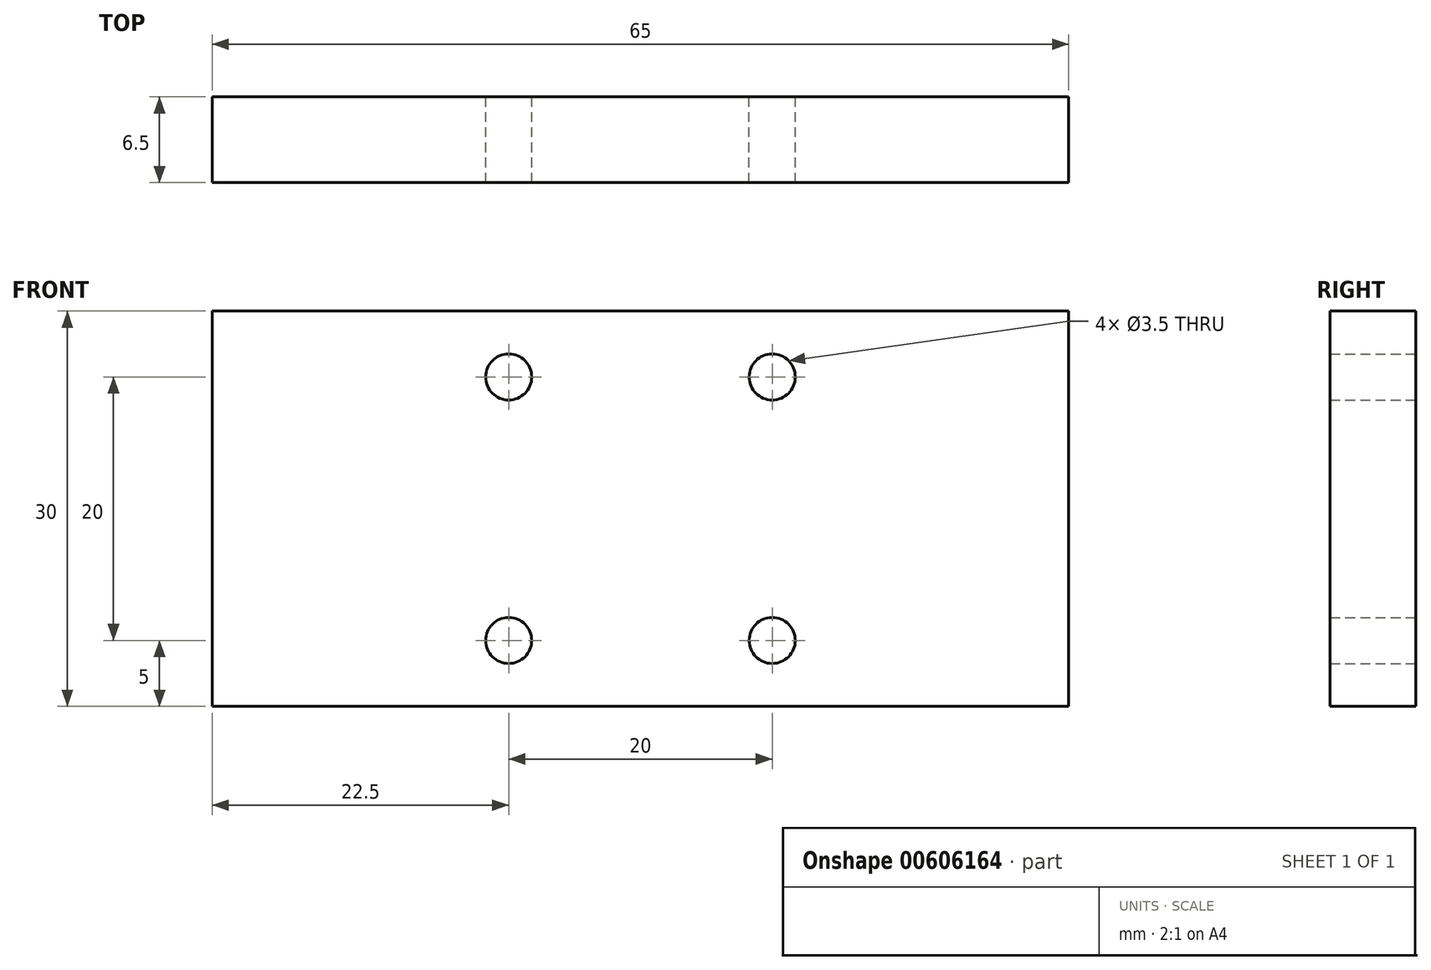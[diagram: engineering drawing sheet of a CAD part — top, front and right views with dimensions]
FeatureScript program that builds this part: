
annotation { "Feature Type Name" : "Feature", "Feature Type Description" : "" }
export const myFeature = defineFeature(function(context is Context, id is Id, definition is map)
    precondition{}
    {
        {
            var Q0;
            Q0=qCreatedBy(makeId("Front.planeOp"),FACE);
            var sketch = newSketch(context, id + "F0", { "sketchPlane" : qUnion([Q0])});
            skLineSegment(sketch, "E0.bottom", {"start": v(32.5, -15) * mm, "end": v(-32.5, -15) * mm});
            skLineSegment(sketch, "E0.top", {"start": v(32.5, 15) * mm, "end": v(-32.5, 15) * mm});
            skLineSegment(sketch, "E0.left", {"start": v(32.5, -15) * mm, "end": v(32.5, 15) * mm});
            skLineSegment(sketch, "E0.right", {"start": v(-32.5, -15) * mm, "end": v(-32.5, 15) * mm});
            skPoint(sketch, "E0.middle", {"position": v(0, 0) * mm});
            skCircle(sketch, "E1", {"center": v(-10, 10) * mm, "radius": 1.75 * mm});
            skCircle(sketch, "E2", {"center": v(-10, -10) * mm, "radius": 1.75 * mm});
            skCircle(sketch, "E3", {"center": v(10, -10) * mm, "radius": 1.75 * mm});
            skCircle(sketch, "E4", {"center": v(10, 10) * mm, "radius": 1.75 * mm});
            skSolve(sketch);
        }
        {
            var Q0;
            Q0=makeQuery(id+"F0.imprint","IMPRINT",FACE,{"disambiguationData":[TD([[makeQuery(id+"F0.imprint","IMPRINT",EDGE,{"derivedFrom":sQuery(id+"F0.wireOp",EDGE,"E0.bottom")}),-1.0]])]});
            extrude(context, id + "F1", {"entities" : qUnion([Q0]), "depth" : 6.5 * mm, "offsetDistance" : 25 * mm});
        }
    });
